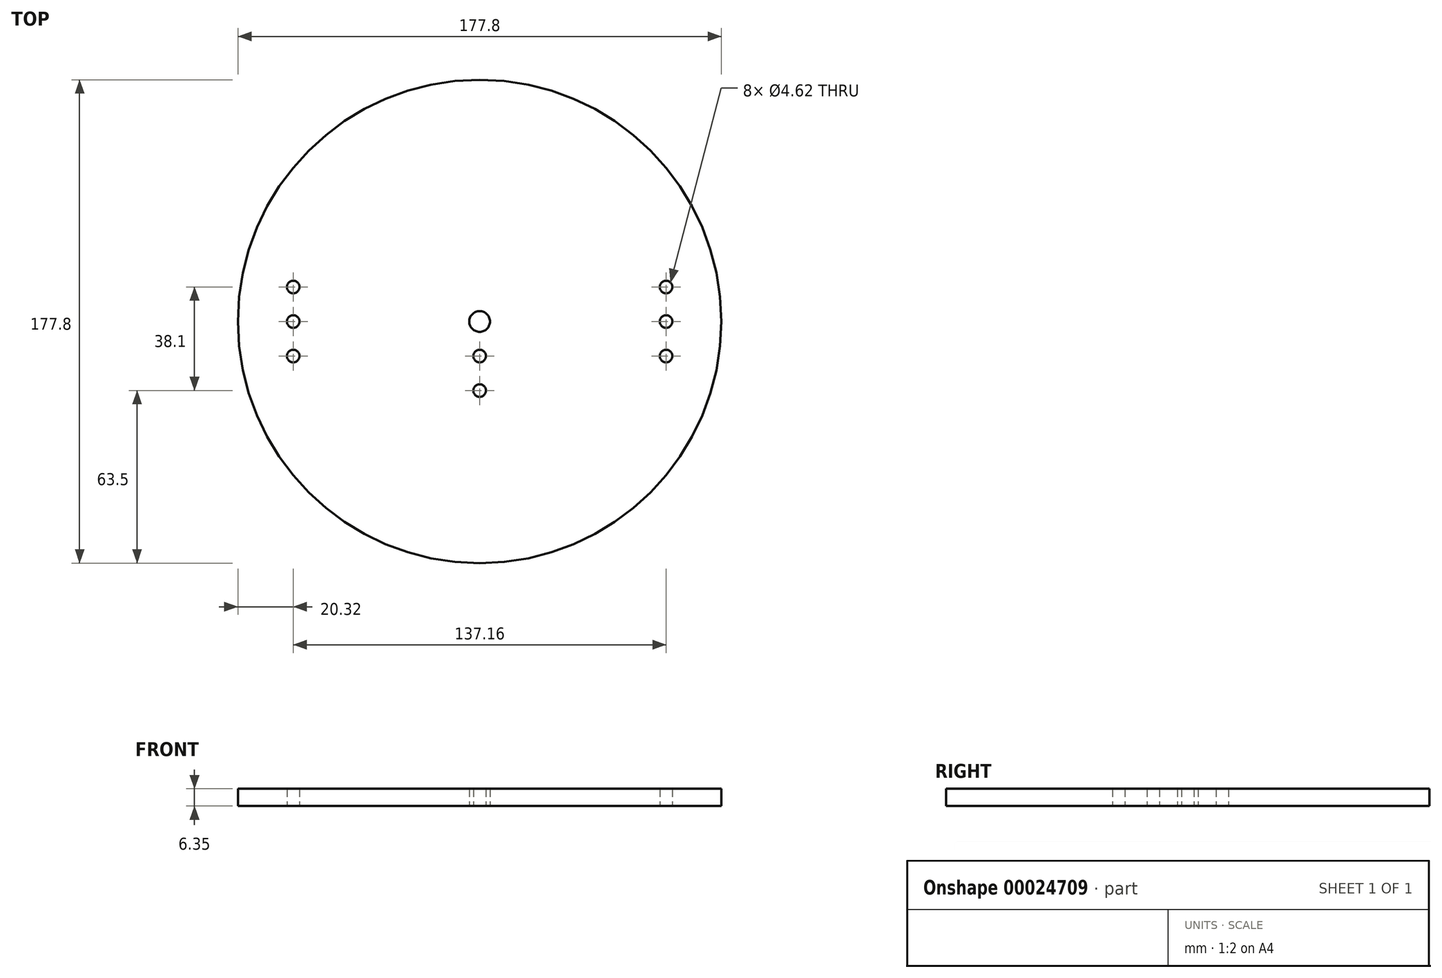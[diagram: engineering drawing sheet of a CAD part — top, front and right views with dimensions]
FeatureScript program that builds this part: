
annotation { "Feature Type Name" : "Feature", "Feature Type Description" : "" }
export const myFeature = defineFeature(function(context is Context, id is Id, definition is map)
    precondition{}
    {
        {
            var Q0;
            Q0=qCreatedBy(makeId("Top.planeOp"),FACE);
            var sketch = newSketch(context, id + "F0", { "sketchPlane" : qUnion([Q0])});
            skCircle(sketch, "E0", {"center": v(0, 0) * mm, "radius": 88.9 * mm});
            skCircle(sketch, "E1", {"center": v(0, 0) * mm, "radius": 3.81 * mm});
            skCircle(sketch, "E2", {"center": v(0, -12.7) * mm, "radius": 2.31 * mm});
            skCircle(sketch, "E3", {"center": v(0, -25.4) * mm, "radius": 2.31 * mm});
            skCircle(sketch, "E4", {"center": v(68.58, -12.7) * mm, "radius": 2.31 * mm});
            skCircle(sketch, "E5", {"center": v(68.58, 12.7) * mm, "radius": 2.31 * mm});
            skCircle(sketch, "E6", {"center": v(68.58, 0) * mm, "radius": 2.31 * mm});
            skCircle(sketch, "E7.1.0.0", {"center": v(-68.58, 12.7) * mm, "radius": 2.31 * mm});
            skCircle(sketch, "E7.1.0.1", {"center": v(-68.58, 0) * mm, "radius": 2.31 * mm});
            skCircle(sketch, "E7.1.0.2", {"center": v(-68.58, -12.7) * mm, "radius": 2.31 * mm});
            skLineSegment(sketch, "E7.direction1", {"start": v(68.58, 12.7) * mm, "end": v(-68.58, 12.7) * mm, "construction": true});
            skSolve(sketch);
        }
        {
            var Q0;
            Q0=makeQuery(id+"F0.imprint","IMPRINT",FACE,{"disambiguationData":[TD([[makeQuery(id+"F0.imprint","IMPRINT",EDGE,{"derivedFrom":sQuery(id+"F0.wireOp",EDGE,"E0")}),1.0]])]});
            extrude(context, id + "F1", {"entities" : qUnion([Q0]), "depth" : 6.35 * mm});
        }
    });
